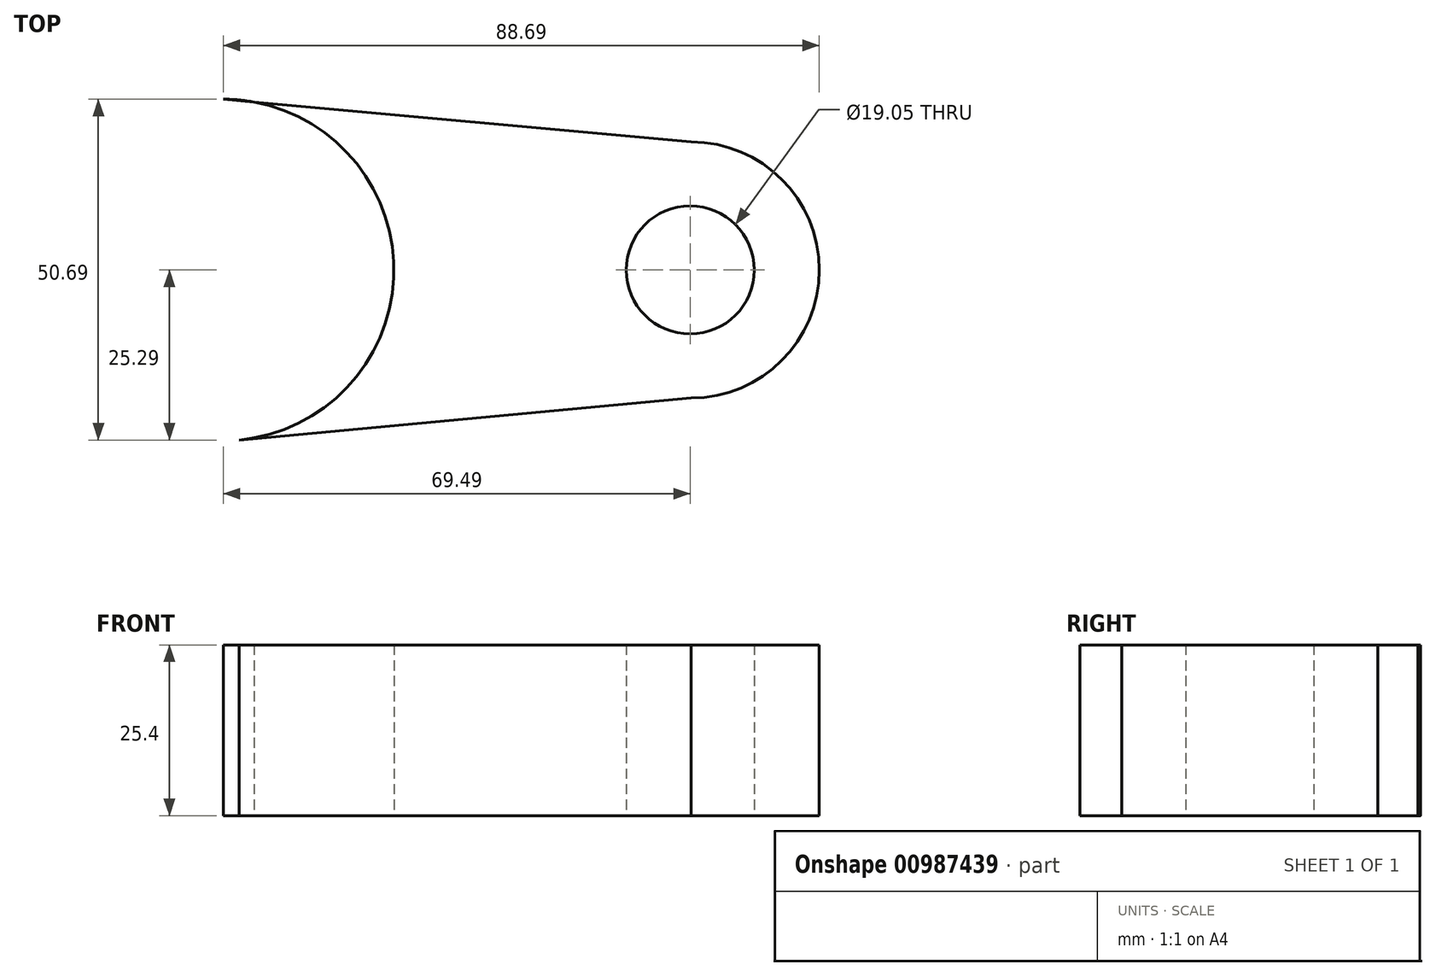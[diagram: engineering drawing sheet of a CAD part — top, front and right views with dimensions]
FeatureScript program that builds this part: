
annotation { "Feature Type Name" : "Feature", "Feature Type Description" : "" }
export const myFeature = defineFeature(function(context is Context, id is Id, definition is map)
    precondition{}
    {
        {
            var Q0;
            Q0=qCreatedBy(makeId("Top.planeOp"),FACE);
            var sketch = newSketch(context, id + "F0", { "sketchPlane" : qUnion([Q0])});
            skCircle(sketch, "E0", {"center": v(0, 0) * mm, "radius": 25.4 * mm});
            skCircle(sketch, "E1", {"center": v(69.64, 0) * mm, "radius": 19.05 * mm});
            skLineSegment(sketch, "E2", {"start": v(0, 25.4) * mm, "end": v(69.64, 19.05) * mm});
            skLineSegment(sketch, "E3", {"start": v(69.64, -19.05) * mm, "end": v(0, -25.5) * mm});
            skSolve(sketch);
        }
        {
            var Q0;
            Q0=qCreatedBy(makeId("Top.planeOp"),FACE);
            var sketch = newSketch(context, id + "F1", { "sketchPlane" : qUnion([Q0])});
            skCircle(sketch, "E4", {"center": v(0, 0) * mm, "radius": 19.05 * mm});
            skCircle(sketch, "E5", {"center": v(145.16, 0) * mm, "radius": 22.8 * mm});
            skCircle(sketch, "E6", {"center": v(69.49, 0) * mm, "radius": 12.7 * mm});
            skSolve(sketch);
        }
        {
            var Q0;
            {var subQ0=sQuery(id+"F0.wireOp",EDGE,"E3");var subQ1=sQuery(id+"F0.wireOp",EDGE,"E0");var subQ2=makeQuery(id+"F0.imprint","INTERSECT",VERTEX,{"derivedFrom":[subQ1,subQ0]});Q0=makeQuery(id+"F0.imprint","IMPRINT",FACE,{"disambiguationData":[TD([[makeQuery(id+"F0.imprint","IMPRINT",EDGE,{"disambiguationData":[TD([[subQ2,-1.0]])],"derivedFrom":subQ1}),-1.0]])]});}
            var Q1;
            {var subQ0=sQuery(id+"F0.wireOp",EDGE,"E2");var subQ1=sQuery(id+"F0.wireOp",EDGE,"E0");var subQ2=makeQuery(id+"F0.imprint","INTERSECT",VERTEX,{"disambiguationData":[OD(0.0)],"derivedFrom":[subQ1,subQ0]});Q1=makeQuery(id+"F0.imprint","IMPRINT",FACE,{"disambiguationData":[TD([[makeQuery(id+"F0.imprint","IMPRINT",EDGE,{"disambiguationData":[TD([[subQ2,-1.0]])],"derivedFrom":subQ1}),1.0]])]});}
            var Q2;
            {var subQ0=sQuery(id+"F0.wireOp",EDGE,"E1");var subQ1=makeQuery(id+"F0.imprint","INTERSECT",VERTEX,{"derivedFrom":[subQ0,sQuery(id+"F0.wireOp",EDGE,"E2")]});Q2=makeQuery(id+"F0.imprint","IMPRINT",FACE,{"disambiguationData":[TD([[makeQuery(id+"F0.imprint","IMPRINT",EDGE,{"disambiguationData":[TD([[subQ1,-1.0]])],"derivedFrom":subQ0}),1.0]])]});}
            extrude(context, id + "F2", {"entities" : qUnion([Q0, Q1, Q2]), "depth" : 25.4 * mm, "offsetDistance" : 25.4 * mm});
        }
        {
            var Q0;
            Q0=sQuery(id+"F1.wireOp",VERTEX,"E4.center");
            var Q1;
            Q1=sQuery(id+"F1.wireOp",VERTEX,"E6.center");
            var Q2;
            Q2=makeQuery(id+"F2.opExtrude","SWEPT_BODY",BODY,{"disambiguationData":[OSD([sQuery(id+"F0.wireOp",EDGE,"E0"),sQuery(id+"F0.wireOp",EDGE,"E1"),sQuery(id+"F0.wireOp",EDGE,"E2"),sQuery(id+"F0.wireOp",EDGE,"E3")])]});
            hole(context, id + "F3", {"style" : HoleStyle.SIMPLE, "endStyle" : HoleEndStyle.BLIND, "oppositeDirection" : true, "holeDiameter" : 19.05 * mm, "majorDiameter" : 6.35 * mm, "holeDepth" : 25.4 * mm, "isTappedThrough" : true, "tappedDepth" : 12.7 * mm, "tapClearance" : 3, "locations" : qUnion([Q0, Q1]), "scope" : qUnion([Q2])});
        }
    });
